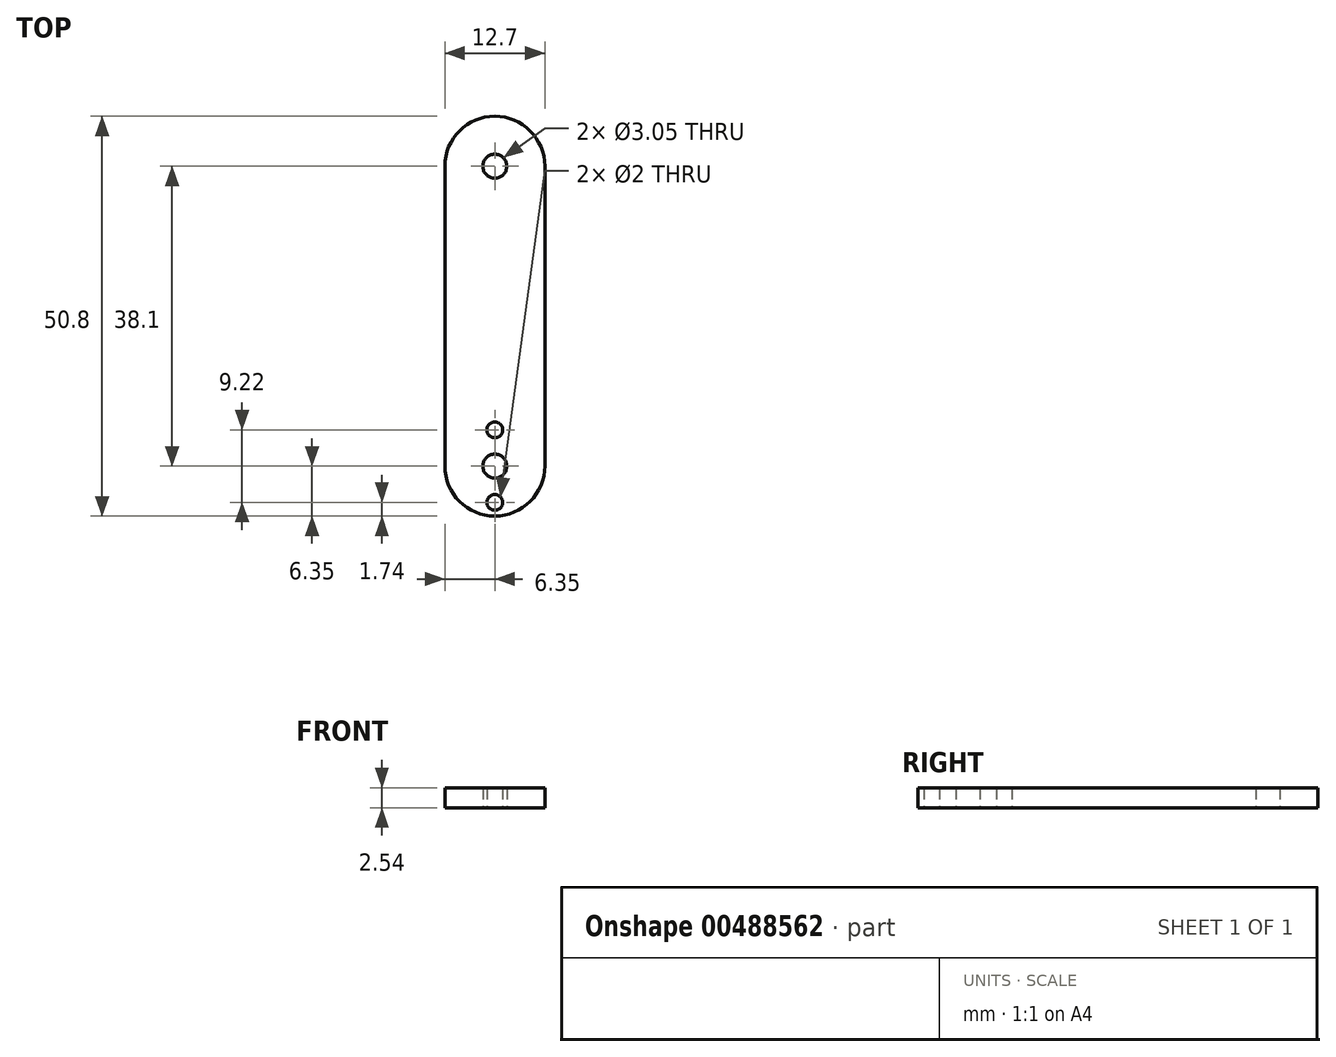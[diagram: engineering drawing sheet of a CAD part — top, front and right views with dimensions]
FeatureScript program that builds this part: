
annotation { "Feature Type Name" : "Feature", "Feature Type Description" : "" }
export const myFeature = defineFeature(function(context is Context, id is Id, definition is map)
    precondition{}
    {
        {
            var Q0;
            Q0=qCreatedBy(makeId("Top.planeOp"),FACE);
            var sketch = newSketch(context, id + "F0", { "sketchPlane" : qUnion([Q0])});
            skLineSegment(sketch, "E0.bottom", {"start": v(0, 25.4) * mm, "end": v(0, 25.4) * mm});
            skLineSegment(sketch, "E0.top", {"start": v(0, -25.4) * mm, "end": v(0, -25.4) * mm});
            skLineSegment(sketch, "E0.left", {"start": v(6.35, 19.05) * mm, "end": v(6.35, -19.05) * mm});
            skLineSegment(sketch, "E0.right", {"start": v(-6.35, 19.05) * mm, "end": v(-6.35, -19.05) * mm});
            skPoint(sketch, "E0.middle", {"position": v(0, 0) * mm});
            skPoint(sketch, "E1.visualSharp", {"position": v(-6.35, 25.4) * mm});
            skArc(sketch, "E1.filletArc", {"start": v(0, 25.4) * mm, "mid": v(-4.5, 23.54) * mm, "end": v(-6.35, 19.05) * mm});
            skPoint(sketch, "E2.visualSharp", {"position": v(6.35, 25.4) * mm});
            skArc(sketch, "E2.filletArc", {"start": v(6.35, 19.05) * mm, "mid": v(4.5, 23.54) * mm, "end": v(0, 25.4) * mm});
            skPoint(sketch, "E3.visualSharp", {"position": v(-6.35, -25.4) * mm});
            skArc(sketch, "E3.filletArc", {"start": v(-6.35, -19.05) * mm, "mid": v(-4.5, -23.54) * mm, "end": v(0, -25.4) * mm});
            skPoint(sketch, "E4.visualSharp", {"position": v(6.35, -25.4) * mm});
            skArc(sketch, "E4.filletArc", {"start": v(0, -25.4) * mm, "mid": v(4.5, -23.54) * mm, "end": v(6.35, -19.05) * mm});
            skCircle(sketch, "E5", {"center": v(0, -19.05) * mm, "radius": 1.52 * mm});
            skCircle(sketch, "E6", {"center": v(0, 19.05) * mm, "radius": 1.52 * mm});
            skCircle(sketch, "E7", {"center": v(0, -14.44) * mm, "radius": 1 * mm});
            skCircle(sketch, "E8", {"center": v(0, -23.66) * mm, "radius": 1 * mm});
            skLineSegment(sketch, "E9", {"start": v(0, -19.05) * mm, "end": v(0, -14.44) * mm, "construction": true});
            skLineSegment(sketch, "E10", {"start": v(0, -19.05) * mm, "end": v(0, -23.66) * mm, "construction": true});
            skSolve(sketch);
        }
        {
            var Q0;
            Q0=makeQuery(id+"F0.imprint","IMPRINT",FACE,{"disambiguationData":[TD([[makeQuery(id+"F0.imprint","IMPRINT",EDGE,{"derivedFrom":sQuery(id+"F0.wireOp",EDGE,"E0.left")}),-1.0]])]});
            extrude(context, id + "F1", {"entities" : qUnion([Q0]), "depth" : 2.54 * mm});
        }
    });
